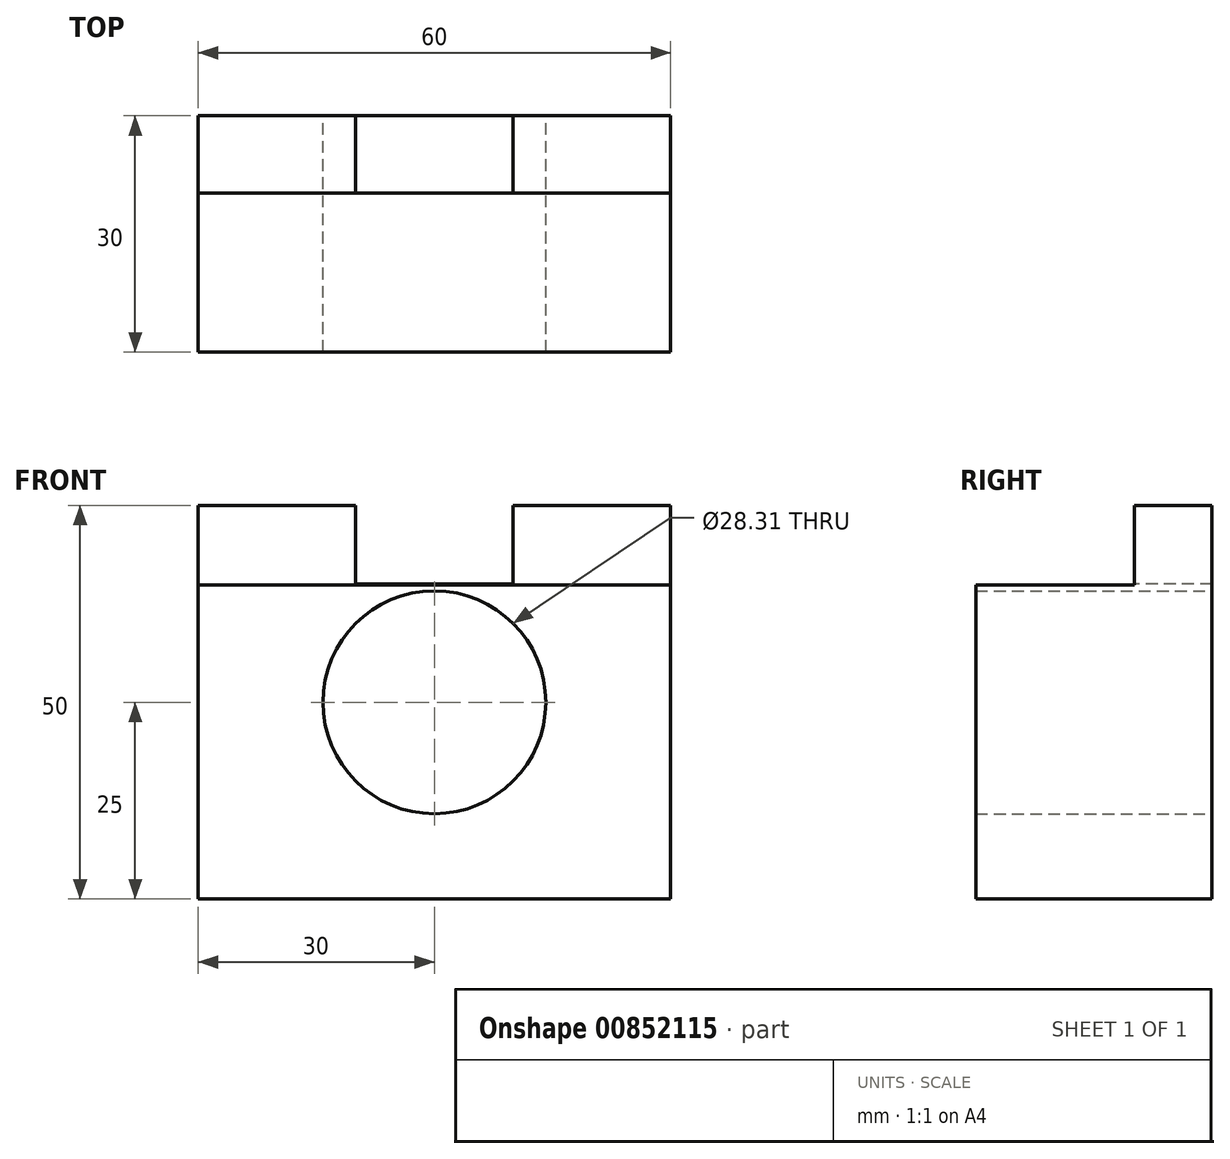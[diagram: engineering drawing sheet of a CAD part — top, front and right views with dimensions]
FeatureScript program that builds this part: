
annotation { "Feature Type Name" : "Feature", "Feature Type Description" : "" }
export const myFeature = defineFeature(function(context is Context, id is Id, definition is map)
    precondition{}
    {
        {
            var Q0;
            Q0=qCreatedBy(makeId("Front.planeOp"),FACE);
            var sketch = newSketch(context, id + "F0", { "sketchPlane" : qUnion([Q0])});
            skLineSegment(sketch, "E0", {"start": v(-30, 0) * mm, "end": v(30, 0) * mm});
            skLineSegment(sketch, "E1", {"start": v(30, 0) * mm, "end": v(30, 50) * mm});
            skLineSegment(sketch, "E2", {"start": v(30, 50) * mm, "end": v(-30, 50) * mm});
            skLineSegment(sketch, "E3", {"start": v(-30, 50) * mm, "end": v(-30, 0) * mm});
            skCircle(sketch, "E4", {"center": v(0, 25) * mm, "radius": 14.15 * mm});
            skPoint(sketch, "E4.centerSnap0", {"position": v(-30, 25) * mm});
            skSolve(sketch);
        }
        {
            var Q0;
            Q0=makeQuery(id+"F0.imprint","IMPRINT",FACE,{"disambiguationData":[TD([[makeQuery(id+"F0.imprint","IMPRINT",EDGE,{"derivedFrom":sQuery(id+"F0.wireOp",EDGE,"E0")}),1.0]])]});
            extrude(context, id + "F1", {"entities" : qUnion([Q0]), "depth" : 30 * mm, "offsetDistance" : 25 * mm});
        }
        {
            var Q0;
            Q0=makeQuery(id+"F1.opExtrude","SWEPT_FACE",FACE,{"disambiguationData":[OSD([sQuery(id+"F0.wireOp",EDGE,"E1")])]});
            var sketch = newSketch(context, id + "F2", { "sketchPlane" : qUnion([Q0])});
            skLineSegment(sketch, "E5", {"start": v(-30, 50) * mm, "end": v(-9.84, 50) * mm});
            skLineSegment(sketch, "E6", {"start": v(-9.84, 50) * mm, "end": v(-9.84, 39.89) * mm});
            skLineSegment(sketch, "E7", {"start": v(-9.84, 39.89) * mm, "end": v(-30, 39.89) * mm});
            skSolve(sketch);
        }
        {
            var Q0;
            {var subQ0=sQuery(id+"F2.wireOp",EDGE,"E5");Q0=makeQuery(id+"F2.imprint","IMPRINT",FACE,{"disambiguationData":[TD([[makeQuery(id+"F2.imprint","IMPRINT",EDGE,{"derivedFrom":subQ0}),-1.0]])]});}
            extrude(context, id + "F3", {"entities" : qUnion([Q0]), "operationType" : NewBodyOperationType.REMOVE, "oppositeDirection" : true, "depth" : 95 * mm, "offsetDistance" : 25 * mm});
        }
        {
            var Q0;
            Q0=makeQuery(id+"F1.opExtrude","SWEPT_FACE",FACE,{"disambiguationData":[OSD([sQuery(id+"F0.wireOp",EDGE,"E2")])]});
            var sketch = newSketch(context, id + "F4", { "sketchPlane" : qUnion([Q0])});
            skLineSegment(sketch, "E8", {"start": v(-30, 0) * mm, "end": v(-10, 0) * mm});
            skLineSegment(sketch, "E9", {"start": v(-10, 0) * mm, "end": v(-10, -9.84) * mm});
            skLineSegment(sketch, "E10", {"start": v(-10, -9.84) * mm, "end": v(10, -9.84) * mm});
            skLineSegment(sketch, "E11", {"start": v(10, -9.84) * mm, "end": v(10, 0) * mm});
            skLineSegment(sketch, "E12", {"start": v(10, 0) * mm, "end": v(30, 0) * mm});
            skSolve(sketch);
        }
        {
            var Q0;
            {var subQ0=sQuery(id+"F4.wireOp",EDGE,"E9");Q0=makeQuery(id+"F4.imprint","IMPRINT",FACE,{"disambiguationData":[TD([[makeQuery(id+"F4.imprint","IMPRINT",EDGE,{"derivedFrom":subQ0}),1.0]])]});}
            extrude(context, id + "F5", {"entities" : qUnion([Q0]), "operationType" : NewBodyOperationType.REMOVE, "oppositeDirection" : true, "depth" : 10 * mm, "offsetDistance" : 25 * mm});
        }
    });
